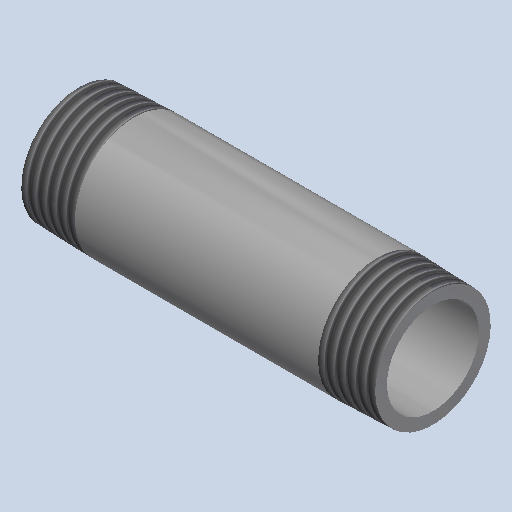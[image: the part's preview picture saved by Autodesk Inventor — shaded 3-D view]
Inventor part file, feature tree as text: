
AUTODESK INVENTOR PART (.ipt)
format: ipt  version: 2025 (Build 290162000, 162)  size: 251,904 bytes
history: native  units: mm (DEFAULTED — no unit token found)
features: other x8, revolve x1
ambient origin geometry x8: Origin, YZ Plane, XZ Plane, XY Plane, X Axis, Y Axis, Z Axis, Center Point
bodies: Solid1 (feature_tree)
feature tree (9):
  revolve  "Revolution1"  [1 undecoded]
  other  "Work Axis1"
  other  "Work Point5"
  other  "Work Axis2"
  other  "Work Point6"
  other  "Work Axis3"
  other  "Work Axis4"
  other  "Work Point7"
  other  "Work Point8"
note: 1 required parameter value undecoded (feature->parameter linkage not recoverable at this tier; creation-order binding heuristic only, values carry confidence <= 0.55)
